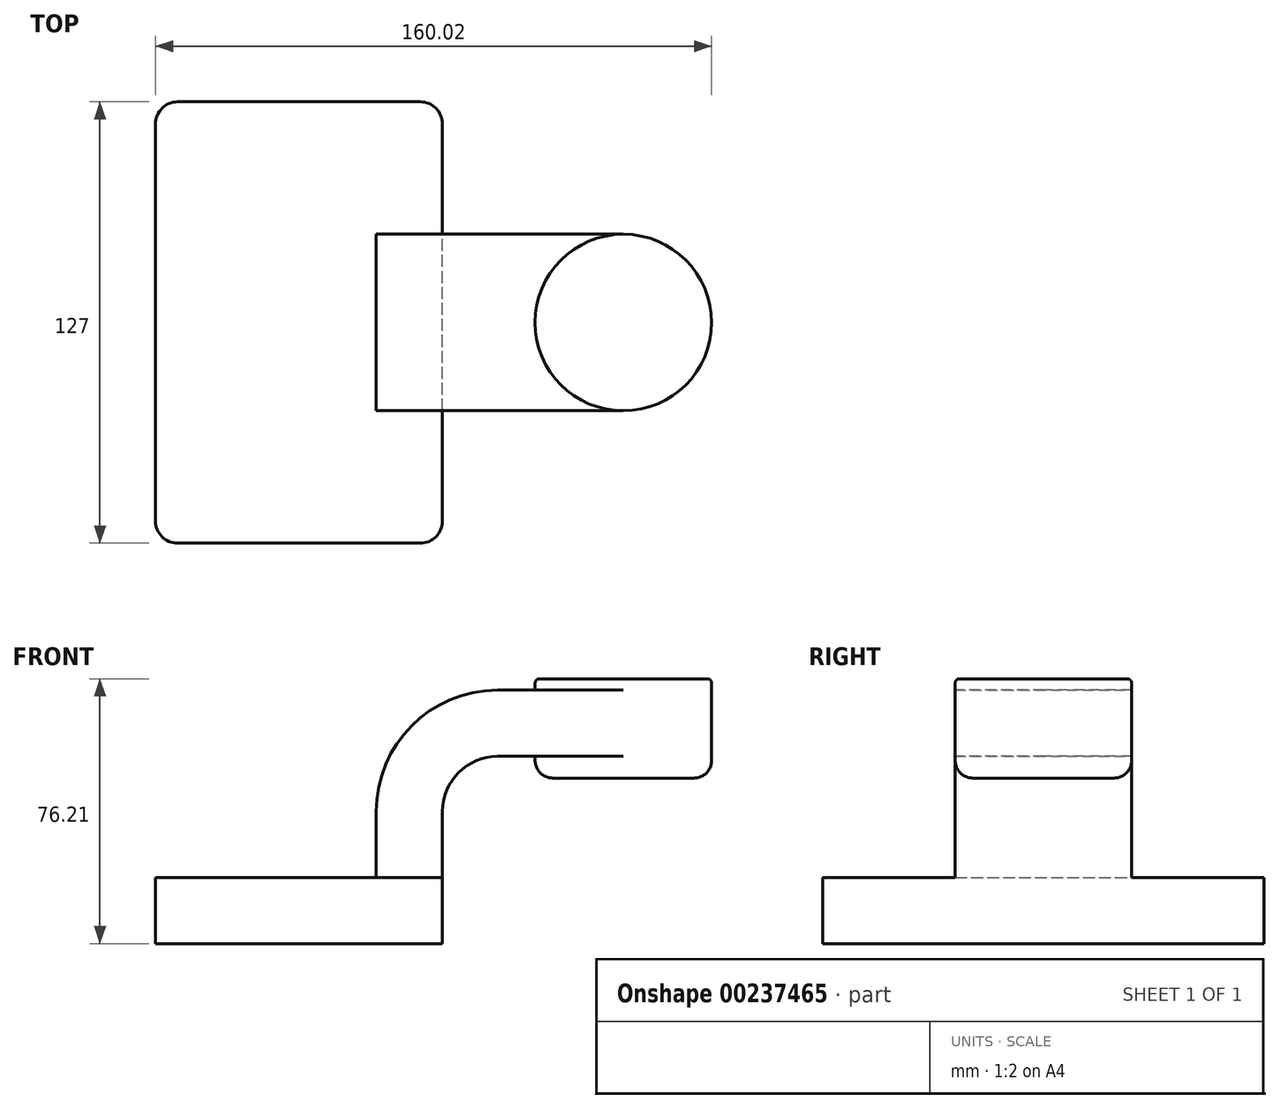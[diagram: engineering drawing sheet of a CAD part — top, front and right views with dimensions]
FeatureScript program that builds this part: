
annotation { "Feature Type Name" : "Feature", "Feature Type Description" : "" }
export const myFeature = defineFeature(function(context is Context, id is Id, definition is map)
    precondition{}
    {
        {
            var Q0;
            Q0=qCreatedBy(makeId("Front.planeOp"),FACE);
            var sketch = newSketch(context, id + "F0", { "sketchPlane" : qUnion([Q0])});
            skLineSegment(sketch, "E0.bottom", {"start": v(-41.28, 9.53) * mm, "end": v(41.28, 9.53) * mm});
            skLineSegment(sketch, "E0.top", {"start": v(-41.28, -9.52) * mm, "end": v(41.28, -9.52) * mm});
            skLineSegment(sketch, "E0.left", {"start": v(-41.28, 9.52) * mm, "end": v(-41.28, -9.53) * mm});
            skLineSegment(sketch, "E0.right", {"start": v(41.28, 9.53) * mm, "end": v(41.28, -9.52) * mm});
            skPoint(sketch, "E0.middle", {"position": v(0, 0) * mm});
            skLineSegment(sketch, "E1", {"start": v(41.28, 9.53) * mm, "end": v(41.28, 28.46) * mm});
            skArc(sketch, "E2", {"start": v(41.28, 28.46) * mm, "mid": v(45.92, 39.68) * mm, "end": v(57.15, 44.33) * mm});
            skLineSegment(sketch, "E3", {"start": v(57.15, 44.33) * mm, "end": v(93.35, 44.33) * mm});
            skLineSegment(sketch, "E4.bottom", {"start": v(67.95, 38.1) * mm, "end": v(118.75, 38.1) * mm});
            skLineSegment(sketch, "E4.top", {"start": v(67.95, 66.67) * mm, "end": v(118.75, 66.67) * mm});
            skLineSegment(sketch, "E4.left", {"start": v(67.95, 38.1) * mm, "end": v(67.95, 66.67) * mm});
            skLineSegment(sketch, "E4.right", {"start": v(118.75, 38.1) * mm, "end": v(118.75, 66.67) * mm});
            skPoint(sketch, "E4.middle", {"position": v(93.35, 52.39) * mm});
            skLineSegment(sketch, "E5.0", {"start": v(57.15, 63.38) * mm, "end": v(93.35, 63.38) * mm});
            skArc(sketch, "E5.1", {"start": v(22.23, 28.46) * mm, "mid": v(32.45, 53.15) * mm, "end": v(57.15, 63.38) * mm});
            skLineSegment(sketch, "E5.2", {"start": v(22.23, 9.53) * mm, "end": v(22.23, 28.46) * mm});
            skFitSpline(sketch, "E6", {"points": [v(-41.28, 9.52) * mm, v(57.15, 63.38) * mm], "startDerivative": vector(1.77, 98.11) * mm, "endDerivative": vector(134.72, -1.04) * mm});
            skLineSegment(sketch, "E7", {"start": v(93.35, 38.1) * mm, "end": v(93.35, 66.68) * mm});
            skSolve(sketch);
        }
        {
            var Q0;
            Q0=makeQuery(id+"F0.imprint","IMPRINT",FACE,{"disambiguationData":[TD([[makeQuery(id+"F0.imprint","IMPRINT",EDGE,{"derivedFrom":sQuery(id+"F0.wireOp",EDGE,"E0.top")}),1.0]])]});
            extrude(context, id + "F1", {"entities" : qUnion([Q0]), "endBound" : BoundingType.SYMMETRIC, "depth" : 127 * mm});
        }
        {
            var Q0;
            {var subQ0=sQuery(id+"F0.wireOp",EDGE,"E7");var subQ1=sQuery(id+"F0.wireOp",EDGE,"E3");var subQ2=makeQuery(id+"F0.imprint","INTERSECT",VERTEX,{"derivedFrom":[subQ1,subQ0]});Q0=makeQuery(id+"F0.imprint","IMPRINT",FACE,{"disambiguationData":[TD([[makeQuery(id+"F0.imprint","IMPRINT",EDGE,{"disambiguationData":[TD([[subQ2,1.0]])],"derivedFrom":subQ1}),1.0]])]});}
            var Q1;
            {var subQ7=sQuery(id+"F0.wireOp",EDGE,"E1");Q1=makeQuery(id+"F0.imprint","IMPRINT",FACE,{"disambiguationData":[TD([[makeQuery(id+"F0.imprint","IMPRINT",EDGE,{"derivedFrom":subQ7}),1.0]])]});}
            extrude(context, id + "F2", {"entities" : qUnion([Q0, Q1]), "operationType" : NewBodyOperationType.ADD, "endBound" : BoundingType.SYMMETRIC, "depth" : 50.8 * mm});
        }
        {
            var Q0;
            Q0=makeQuery(id+"F0.imprint","IMPRINT",FACE,{"disambiguationData":[TD([[makeQuery(id+"F0.imprint","IMPRINT",EDGE,{"derivedFrom":sQuery(id+"F0.wireOp",EDGE,"E5.1")}),1.0]])]});
            extrude(context, id + "F3", {"entities" : qUnion([Q0]), "operationType" : NewBodyOperationType.ADD, "endBound" : BoundingType.SYMMETRIC, "depth" : 16.5 * mm});
        }
        {
            var Q0;
            {var subQ5=sQuery(id+"F0.wireOp",EDGE,"E4.right");Q0=makeQuery(id+"F0.imprint","IMPRINT",FACE,{"disambiguationData":[TD([[makeQuery(id+"F0.imprint","IMPRINT",EDGE,{"derivedFrom":subQ5}),1.0]])]});}
            var Q1;
            Q1=sQuery(id+"F0.wireOp",EDGE,"E7");
            revolve(context, id + "F4", {"operationType" : NewBodyOperationType.ADD, "entities" : qUnion([Q0]), "axis" : qUnion([Q1]), "revolveType" : RevolveType.FULL});
        }
        {
            var Q0;
            Q0=makeQuery(id+"F1.opExtrude","CAP_EDGE",EDGE,{"disambiguationData":[OSD([sQuery(id+"F0.wireOp",EDGE,"E0.right")])],"isStart":false});
            var Q1;
            Q1=makeQuery(id+"F1.opExtrude","CAP_EDGE",EDGE,{"disambiguationData":[OSD([sQuery(id+"F0.wireOp",EDGE,"E0.left")])],"isStart":false});
            var Q2;
            Q2=makeQuery(id+"F1.opExtrude","CAP_EDGE",EDGE,{"disambiguationData":[OSD([sQuery(id+"F0.wireOp",EDGE,"E0.left")])],"isStart":true});
            var Q3;
            Q3=makeQuery(id+"F1.opExtrude","CAP_EDGE",EDGE,{"disambiguationData":[OSD([sQuery(id+"F0.wireOp",EDGE,"E0.right")])],"isStart":true});
            fillet(context, id + "F5", {"entities" : qUnion([Q0, Q1, Q2, Q3]), "radius" : 6.35 * mm, "tangentPropagation" : true, "allowEdgeOverflow" : false});
        }
        {
            var Q0;
            Q0=makeQuery(id+"F4.opRevolve","SWEPT_EDGE",EDGE,{"disambiguationData":[OSD([sQuery(id+"F0.wireOp",EDGE,"E4.top"),sQuery(id+"F0.wireOp",EDGE,"E4.right")])]});
            fillet(context, id + "F6", {"entities" : qUnion([Q0]), "radius" : 1.27 * mm, "tangentPropagation" : true, "allowEdgeOverflow" : false});
        }
        {
            var Q0;
            Q0=makeQuery(id+"F4.opRevolve","SWEPT_EDGE",EDGE,{"disambiguationData":[OSD([sQuery(id+"F0.wireOp",EDGE,"E4.bottom"),sQuery(id+"F0.wireOp",EDGE,"E4.right")])]});
            fillet(context, id + "F7", {"entities" : qUnion([Q0]), "radius" : 5.08 * mm, "tangentPropagation" : true, "allowEdgeOverflow" : false});
        }
    });
